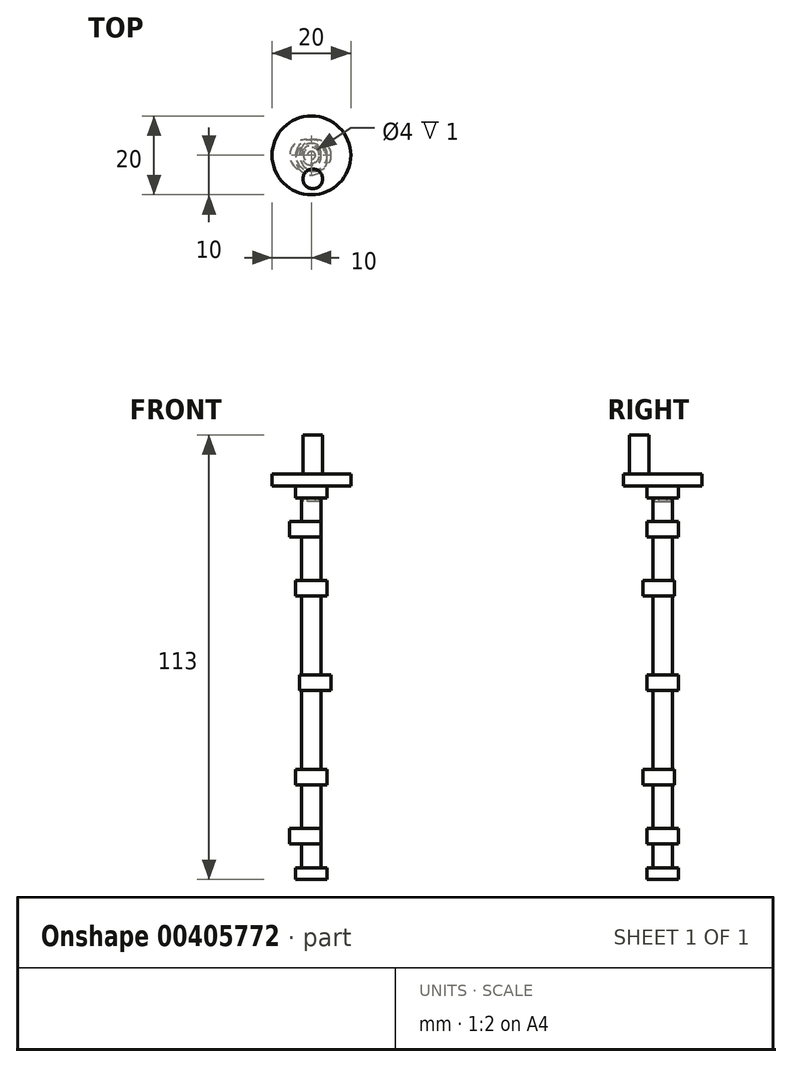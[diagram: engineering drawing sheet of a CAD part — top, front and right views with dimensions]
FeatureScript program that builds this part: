
annotation { "Feature Type Name" : "Feature", "Feature Type Description" : "" }
export const myFeature = defineFeature(function(context is Context, id is Id, definition is map)
    precondition{}
    {
        {
            var Q0;
            Q0=qCreatedBy(makeId("Top.planeOp"),FACE);
            var sketch = newSketch(context, id + "F0", { "sketchPlane" : qUnion([Q0])});
            skCircle(sketch, "E0", {"center": v(0, 0) * mm, "radius": 4 * mm});
            skSolve(sketch);
        }
        {
            var Q0;
            Q0=makeQuery(id+"F0.imprint","IMPRINT",FACE,{"disambiguationData":[TD([[makeQuery(id+"F0.imprint","IMPRINT",EDGE,{"derivedFrom":sQuery(id+"F0.wireOp",EDGE,"E0")}),1.0]])]});
            extrude(context, id + "F1", {"entities" : qUnion([Q0]), "depth" : 3 * mm, "hasSecondDirection" : true, "secondDirectionOppositeDirection" : true, "secondDirectionDepth" : 1 * mm, "offsetDistance" : 25 * mm});
        }
        {
            var Q0;
            Q0=qCreatedBy(makeId("Top.planeOp"),FACE);
            var sketch = newSketch(context, id + "F2", { "sketchPlane" : qUnion([Q0])});
            skCircle(sketch, "E1", {"center": v(0, 0) * mm, "radius": 2.5 * mm});
            skSolve(sketch);
        }
        {
            var Q0;
            Q0=makeQuery(id+"F2.imprint","IMPRINT",FACE,{"disambiguationData":[TD([[makeQuery(id+"F2.imprint","IMPRINT",EDGE,{"derivedFrom":sQuery(id+"F2.wireOp",EDGE,"E1")}),1.0]])]});
            extrude(context, id + "F3", {"entities" : qUnion([Q0]), "operationType" : NewBodyOperationType.ADD, "oppositeDirection" : true, "depth" : 98 * mm, "offsetDistance" : 25 * mm});
        }
        {
            var Q0;
            Q0=qCreatedBy(makeId("Top.planeOp"),FACE);
            cPlane(context, id + "F4", {"entities" : qUnion([Q0]), "cplaneType" : CPlaneType.OFFSET, "offset" : 50 * mm, "oppositeDirection" : true, "width" : 150 * mm, "height" : 150 * mm});
        }
        {
            var Q0;
            Q0=qCreatedBy(id+"F4.planeOp",FACE);
            var sketch = newSketch(context, id + "F5", { "sketchPlane" : qUnion([Q0])});
            skLineSegment(sketch, "E2", {"start": v(0, 0) * mm, "end": v(1, 0) * mm});
            skCircle(sketch, "E3", {"center": v(1, 0) * mm, "radius": 4 * mm});
            skSolve(sketch);
        }
        {
            var Q0;
            Q0=makeQuery(id+"F5.imprint","IMPRINT",FACE,{"disambiguationData":[TD([[makeQuery(id+"F5.imprint","IMPRINT",EDGE,{"derivedFrom":sQuery(id+"F5.wireOp",EDGE,"E3")}),1.0]])]});
            extrude(context, id + "F6", {"entities" : qUnion([Q0]), "operationType" : NewBodyOperationType.ADD, "depth" : 4 * mm});
        }
        {
            var Q0;
            Q0=qCreatedBy(makeId("Top.planeOp"),FACE);
            cPlane(context, id + "F7", {"entities" : qUnion([Q0]), "cplaneType" : CPlaneType.OFFSET, "offset" : 26 * mm, "oppositeDirection" : true, "width" : 150 * mm, "height" : 150 * mm});
        }
        {
            var Q0;
            Q0=qCreatedBy(id+"F7.planeOp",FACE);
            var sketch = newSketch(context, id + "F8", { "sketchPlane" : qUnion([Q0])});
            skLineSegment(sketch, "E4", {"start": v(0, 0) * mm, "end": v(0, -1) * mm, "construction": true});
            skCircle(sketch, "E5", {"center": v(0, -1) * mm, "radius": 4 * mm});
            skSolve(sketch);
        }
        {
            var Q0;
            Q0=makeQuery(id+"F8.imprint","IMPRINT",FACE,{"disambiguationData":[TD([[makeQuery(id+"F8.imprint","IMPRINT",EDGE,{"derivedFrom":sQuery(id+"F8.wireOp",EDGE,"thWs2gKH-3rqn-kz7j-wUtc-lvp8BJZoEOdn")}),1.0]])]});
            var Q1;
            Q1=makeQuery(id+"F8.imprint","IMPRINT",FACE,{"disambiguationData":[TD([[makeQuery(id+"F8.imprint","IMPRINT",EDGE,{"derivedFrom":sQuery(id+"F8.wireOp",EDGE,"E5")}),1.0]])]});
            extrude(context, id + "F9", {"entities" : qUnion([Q0, Q1]), "operationType" : NewBodyOperationType.ADD, "depth" : 4 * mm, "offsetDistance" : 25 * mm});
        }
        {
            var Q0;
            Q0=qCreatedBy(makeId("Top.planeOp"),FACE);
            cPlane(context, id + "F10", {"entities" : qUnion([Q0]), "cplaneType" : CPlaneType.OFFSET, "offset" : 11 * mm, "oppositeDirection" : true, "width" : 150 * mm, "height" : 150 * mm});
        }
        {
            var Q0;
            Q0=qCreatedBy(id+"F10.planeOp",FACE);
            var sketch = newSketch(context, id + "F11", { "sketchPlane" : qUnion([Q0])});
            skLineSegment(sketch, "E6", {"start": v(0, 0) * mm, "end": v(-1.5, 0) * mm});
            skCircle(sketch, "E7", {"center": v(-1.5, 0) * mm, "radius": 4 * mm});
            skSolve(sketch);
        }
        {
            var Q0;
            Q0=makeQuery(id+"F11.imprint","IMPRINT",FACE,{"disambiguationData":[TD([[makeQuery(id+"F11.imprint","IMPRINT",EDGE,{"derivedFrom":sQuery(id+"F11.wireOp",EDGE,"IiB8xn1i-FdeQ-rCM5-RWI7-HBvruacnjr4L")}),1.0]])]});
            var Q1;
            Q1=makeQuery(id+"F11.imprint","IMPRINT",FACE,{"disambiguationData":[TD([[makeQuery(id+"F11.imprint","IMPRINT",EDGE,{"derivedFrom":sQuery(id+"F11.wireOp",EDGE,"E7")}),1.0]])]});
            extrude(context, id + "F12", {"entities" : qUnion([Q0, Q1]), "operationType" : NewBodyOperationType.ADD, "depth" : 4 * mm, "offsetDistance" : 25 * mm});
        }
        {
            var Q0;
            Q0=qCreatedBy(makeId("Top.planeOp"),FACE);
            cPlane(context, id + "F13", {"entities" : qUnion([Q0]), "cplaneType" : CPlaneType.OFFSET, "offset" : 74 * mm, "oppositeDirection" : true, "width" : 150 * mm, "height" : 150 * mm});
        }
        {
            var Q0;
            Q0=qCreatedBy(id+"F13.planeOp",FACE);
            var sketch = newSketch(context, id + "F14", { "sketchPlane" : qUnion([Q0])});
            skLineSegment(sketch, "E8", {"start": v(0, 0) * mm, "end": v(0, -1) * mm});
            skCircle(sketch, "E9", {"center": v(0, -1) * mm, "radius": 4 * mm});
            skSolve(sketch);
        }
        {
            var Q0;
            Q0 = qSketchRegion(id + "F14", true);
            extrude(context, id + "F15", {"entities" : qUnion([Q0]), "operationType" : NewBodyOperationType.ADD, "depth" : 4 * mm});
        }
        {
            var Q0;
            Q0=qCreatedBy(makeId("Top.planeOp"),FACE);
            cPlane(context, id + "F16", {"entities" : qUnion([Q0]), "cplaneType" : CPlaneType.OFFSET, "offset" : 89 * mm, "oppositeDirection" : true, "width" : 150 * mm, "height" : 150 * mm});
        }
        {
            var Q0;
            Q0=qCreatedBy(id+"F16.planeOp",FACE);
            var sketch = newSketch(context, id + "F17", { "sketchPlane" : qUnion([Q0])});
            skLineSegment(sketch, "E10", {"start": v(0, 0) * mm, "end": v(-1.5, 0) * mm});
            skCircle(sketch, "E11", {"center": v(-1.5, 0) * mm, "radius": 4 * mm});
            skSolve(sketch);
        }
        {
            var Q0;
            Q0=makeQuery(id+"F17.imprint","IMPRINT",FACE,{"disambiguationData":[TD([[makeQuery(id+"F17.imprint","IMPRINT",EDGE,{"derivedFrom":sQuery(id+"F17.wireOp",EDGE,"E11")}),1.0]])]});
            extrude(context, id + "F18", {"entities" : qUnion([Q0]), "operationType" : NewBodyOperationType.ADD, "depth" : 4 * mm});
        }
        {
            var Q0;
            Q0=qCreatedBy(makeId("Top.planeOp"),FACE);
            var sketch = newSketch(context, id + "F19", { "sketchPlane" : qUnion([Q0])});
            skCircle(sketch, "E12", {"center": v(0, 0) * mm, "radius": 10 * mm});
            skSolve(sketch);
        }
        {
            var Q0;
            Q0=makeQuery(id+"F19.imprint","IMPRINT",FACE,{"disambiguationData":[TD([[makeQuery(id+"F19.imprint","IMPRINT",EDGE,{"derivedFrom":sQuery(id+"F19.wireOp",EDGE,"E12")}),1.0]])]});
            extrude(context, id + "F20", {"entities" : qUnion([Q0]), "operationType" : NewBodyOperationType.ADD, "depth" : 5 * mm, "hasSecondDirection" : true, "secondDirectionOppositeDirection" : false, "secondDirectionDepth" : 2 * mm});
        }
        {
            var Q0;
            Q0=makeQuery(id+"F20.opExtrude","CAP_FACE",FACE,{"disambiguationData":[OSD([sQuery(id+"F19.wireOp",EDGE,"E12")])],"isStart":false});
            var sketch = newSketch(context, id + "F21", { "sketchPlane" : qUnion([Q0])});
            skLineSegment(sketch, "E13", {"start": v(0, 0) * mm, "end": v(0.35, -5.99) * mm, "construction": true});
            skCircle(sketch, "E14", {"center": v(0.35, -5.99) * mm, "radius": 2.5 * mm});
            skSolve(sketch);
        }
        {
            var Q0;
            Q0=makeQuery(id+"F21.imprint","IMPRINT",FACE,{"disambiguationData":[TD([[makeQuery(id+"F21.imprint","IMPRINT",EDGE,{"derivedFrom":sQuery(id+"F21.wireOp",EDGE,"E14")}),1.0]])]});
            extrude(context, id + "F22", {"entities" : qUnion([Q0]), "operationType" : NewBodyOperationType.ADD, "depth" : 10 * mm});
        }
        {
            var Q0;
            Q0=qCreatedBy(makeId("Top.planeOp"),FACE);
            cPlane(context, id + "F23", {"entities" : qUnion([Q0]), "cplaneType" : CPlaneType.OFFSET, "offset" : 1 * mm, "oppositeDirection" : true, "width" : 150 * mm, "height" : 150 * mm});
        }
        {
            var Q0;
            Q0=qCreatedBy(id+"F23.planeOp",FACE);
            var sketch = newSketch(context, id + "F24", { "sketchPlane" : qUnion([Q0])});
            skCircle(sketch, "E15", {"center": v(0, 0) * mm, "radius": 1 * mm});
            skCircle(sketch, "E16", {"center": v(0, 0) * mm, "radius": 2 * mm});
            skSolve(sketch);
        }
        {
            var Q0;
            Q0 = qSketchRegion(id + "F24", true);
            extrude(context, id + "F25", {"entities" : qUnion([Q0]), "operationType" : NewBodyOperationType.REMOVE, "oppositeDirection" : true, "depth" : 1 * mm, "offsetDistance" : 25 * mm});
        }
        {
            var Q0;
            Q0=makeQuery(id+"F3.opExtrude","CAP_FACE",FACE,{"disambiguationData":[OSD([sQuery(id+"F2.wireOp",EDGE,"E1")])],"isStart":false});
            var sketch = newSketch(context, id + "F26", { "sketchPlane" : qUnion([Q0])});
            skCircle(sketch, "E17", {"center": v(0, 0) * mm, "radius": 4 * mm});
            skSolve(sketch);
        }
        {
            var Q0;
            Q0=makeQuery(id+"F26.imprint","IMPRINT",FACE,{"disambiguationData":[TD([[makeQuery(id+"F26.imprint","IMPRINT",EDGE,{"derivedFrom":sQuery(id+"F26.wireOp",EDGE,"E17")}),1.0]])]});
            extrude(context, id + "F27", {"entities" : qUnion([Q0]), "operationType" : NewBodyOperationType.ADD, "oppositeDirection" : true, "depth" : 3 * mm, "offsetDistance" : 25 * mm});
        }
    });
